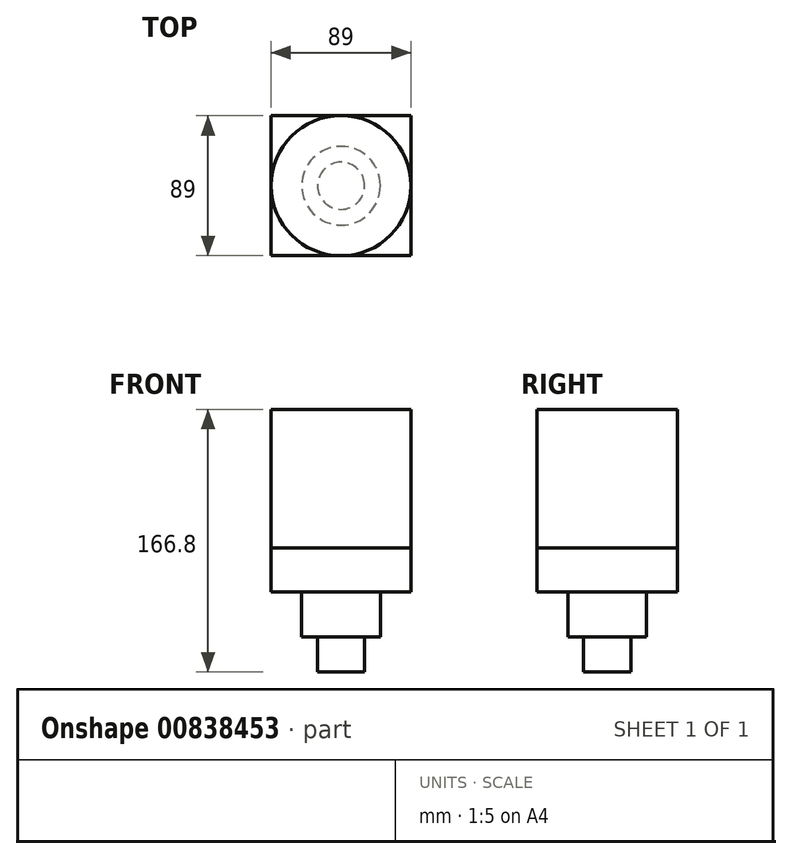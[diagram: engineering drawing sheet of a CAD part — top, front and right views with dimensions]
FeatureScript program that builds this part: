
annotation { "Feature Type Name" : "Feature", "Feature Type Description" : "" }
export const myFeature = defineFeature(function(context is Context, id is Id, definition is map)
    precondition{}
    {
        {
            var Q0;
            Q0=qCreatedBy(makeId("Top.planeOp"),FACE);
            var sketch = newSketch(context, id + "F0", { "sketchPlane" : qUnion([Q0])});
            skLineSegment(sketch, "E0.bottom", {"start": v(44.5, -44.5) * mm, "end": v(-44.5, -44.5) * mm});
            skLineSegment(sketch, "E0.top", {"start": v(44.5, 44.5) * mm, "end": v(-44.5, 44.5) * mm});
            skLineSegment(sketch, "E0.left", {"start": v(44.5, -44.5) * mm, "end": v(44.5, 44.5) * mm});
            skLineSegment(sketch, "E0.right", {"start": v(-44.5, -44.5) * mm, "end": v(-44.5, 44.5) * mm});
            skPoint(sketch, "E0.middle", {"position": v(0, 0) * mm});
            skCircle(sketch, "E1", {"center": v(0, 0) * mm, "radius": 44.5 * mm});
            skCircle(sketch, "E2", {"center": v(0, 0) * mm, "radius": 25 * mm});
            skCircle(sketch, "E3", {"center": v(0, 0) * mm, "radius": 15 * mm});
            skSolve(sketch);
        }
        {
            var Q0;
            Q0 = qSketchRegion(id + "F0", true);
            var Q1;
            {var subQ0=sQuery(id+"F0.wireOp",EDGE,"E0.right");var subQ1=sQuery(id+"F0.wireOp",EDGE,"E0.top");var subQ2=makeQuery(id+"F0.imprint","INTERSECT",VERTEX,{"derivedFrom":[subQ1,subQ0]});Q1=makeQuery(id+"F0.imprint","IMPRINT",FACE,{"disambiguationData":[TD([[makeQuery(id+"F0.imprint","IMPRINT",EDGE,{"disambiguationData":[TD([[subQ2,1.0]])],"derivedFrom":subQ1}),1.0]])]});}
            var Q2;
            Q2=makeQuery(id+"F0.imprint","IMPRINT",FACE,{"disambiguationData":[TD([[makeQuery(id+"F0.imprint","IMPRINT",EDGE,{"derivedFrom":sQuery(id+"F0.wireOp",EDGE,"E2")}),1.0]])]});
            extrude(context, id + "F1", {"entities" : qUnion([Q0, Q1, Q2]), "depth" : 28 * mm, "offsetDistance" : 25 * mm});
        }
        {
            var Q0;
            Q0=makeQuery(id+"F0.imprint","IMPRINT",FACE,{"disambiguationData":[TD([[makeQuery(id+"F0.imprint","IMPRINT",EDGE,{"derivedFrom":sQuery(id+"F0.wireOp",EDGE,"E2")}),-1.0]])]});
            var Q1;
            Q1=makeQuery(id+"F0.imprint","IMPRINT",FACE,{"disambiguationData":[TD([[makeQuery(id+"F0.imprint","IMPRINT",EDGE,{"derivedFrom":sQuery(id+"F0.wireOp",EDGE,"E2")}),1.0]])]});
            var Q2;
            Q2=makeQuery(id+"F0.imprint","IMPRINT",FACE,{"disambiguationData":[TD([[makeQuery(id+"F0.imprint","IMPRINT",EDGE,{"derivedFrom":sQuery(id+"F0.wireOp",EDGE,"E3")}),1.0]])]});
            extrude(context, id + "F2", {"entities" : qUnion([Q0, Q1, Q2]), "operationType" : NewBodyOperationType.ADD, "depth" : 116 * mm, "offsetDistance" : 25 * mm});
        }
        {
            var Q0;
            Q0=makeQuery(id+"F0.imprint","IMPRINT",FACE,{"disambiguationData":[TD([[makeQuery(id+"F0.imprint","IMPRINT",EDGE,{"derivedFrom":sQuery(id+"F0.wireOp",EDGE,"E2")}),1.0]])]});
            extrude(context, id + "F3", {"entities" : qUnion([Q0]), "operationType" : NewBodyOperationType.ADD, "oppositeDirection" : true, "depth" : 28.5 * mm, "offsetDistance" : 25 * mm});
        }
        {
            var Q0;
            Q0=makeQuery(id+"F0.imprint","IMPRINT",FACE,{"disambiguationData":[TD([[makeQuery(id+"F0.imprint","IMPRINT",EDGE,{"derivedFrom":sQuery(id+"F0.wireOp",EDGE,"E3")}),1.0]])]});
            extrude(context, id + "F4", {"entities" : qUnion([Q0]), "operationType" : NewBodyOperationType.ADD, "oppositeDirection" : true, "depth" : 50.8 * mm, "offsetDistance" : 25 * mm});
        }
    });
